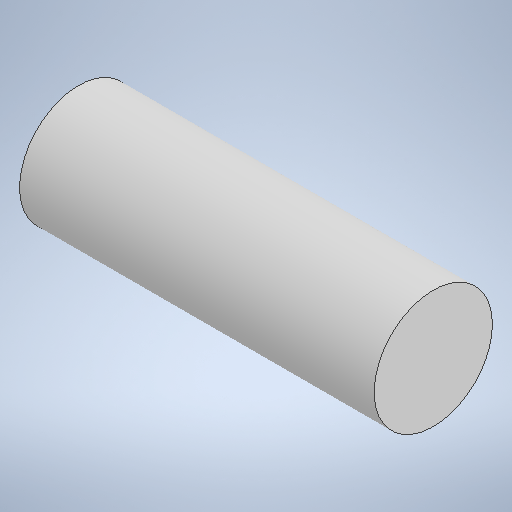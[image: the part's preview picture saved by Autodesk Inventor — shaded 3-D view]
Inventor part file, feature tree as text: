
AUTODESK INVENTOR PART (.ipt)
format: ipt  version: 2025.1 (Build 291241000, 241)  size: 251,904 bytes
history: native  units: mm
features: revolve x1, sketch x1
ambient origin geometry x8: Origin, YZ Plane, XZ Plane, XY Plane, X Axis, Y Axis, Z Axis, Center Point
bodies: Solid1 (feature_tree)
feature tree (2):
  revolve  "Revolution1"  [1 undecoded]
  sketch  "Sketch1"  dims[d0=4.0mm d1=12.0mm d2=90.0deg]
note: 1 required parameter value undecoded (feature->parameter linkage not recoverable at this tier; creation-order binding heuristic only, values carry confidence <= 0.55)
